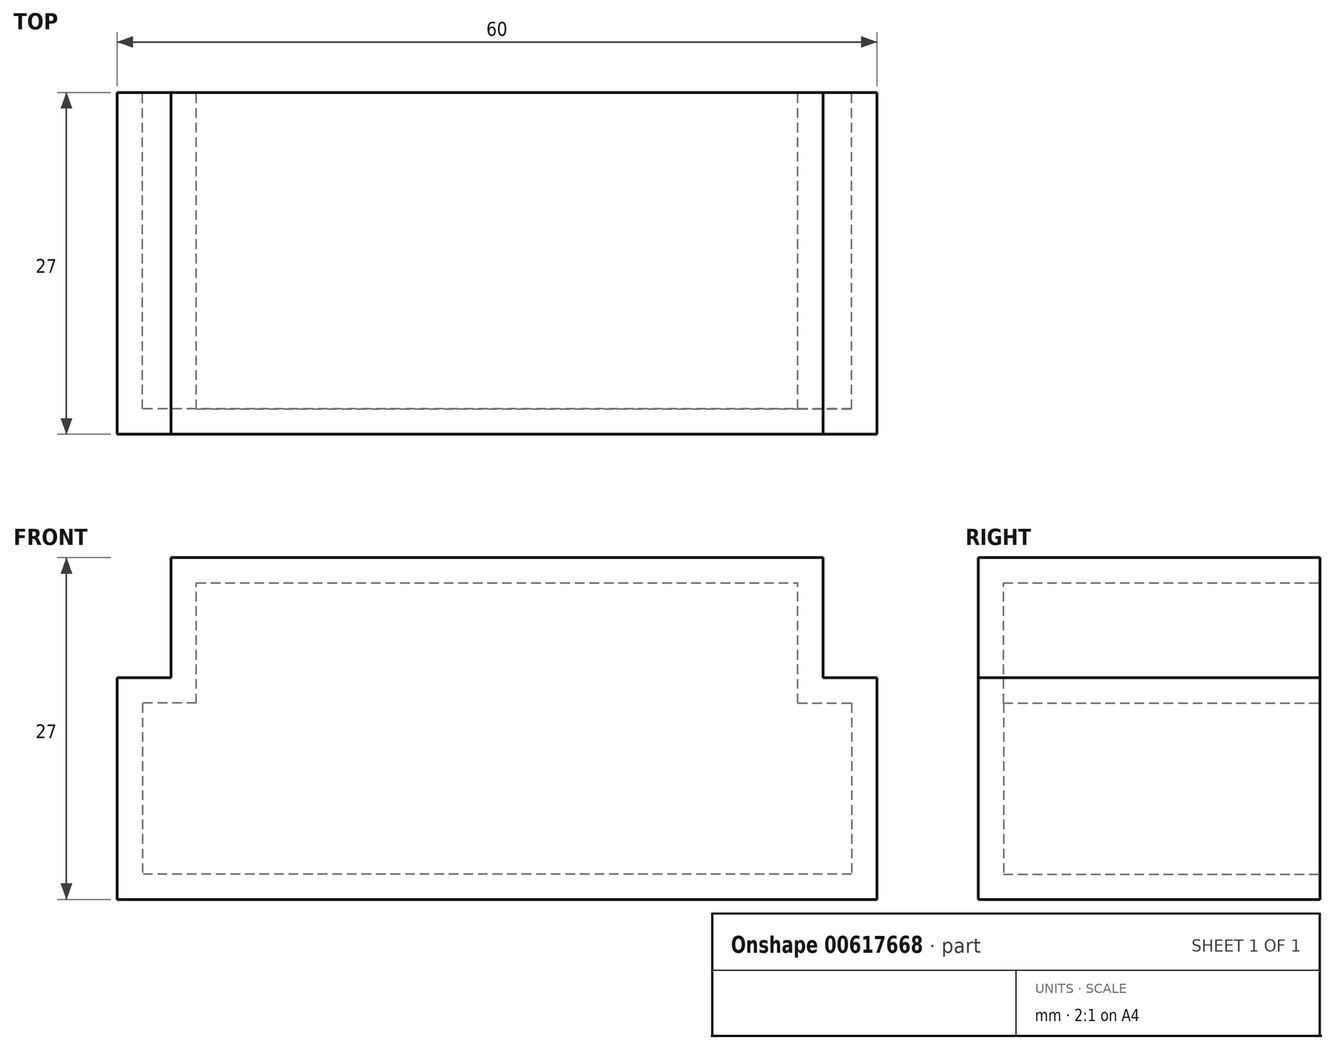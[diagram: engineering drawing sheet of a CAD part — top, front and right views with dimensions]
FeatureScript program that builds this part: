
annotation { "Feature Type Name" : "Feature", "Feature Type Description" : "" }
export const myFeature = defineFeature(function(context is Context, id is Id, definition is map)
    precondition{}
    {
        {
            var Q0;
            Q0=qCreatedBy(makeId("Front.planeOp"),FACE);
            var sketch = newSketch(context, id + "F0", { "sketchPlane" : qUnion([Q0])});
            skLineSegment(sketch, "E0.bottom", {"start": v(0, 0) * mm, "end": v(47.5, 0) * mm});
            skLineSegment(sketch, "E0.top", {"start": v(0, 9.5) * mm, "end": v(47.5, 9.5) * mm});
            skLineSegment(sketch, "E0.left", {"start": v(0, 0) * mm, "end": v(0, 9.5) * mm});
            skLineSegment(sketch, "E0.right", {"start": v(47.5, 0) * mm, "end": v(47.5, 9.5) * mm});
            skLineSegment(sketch, "E1.bottom", {"start": v(0, 9.5) * mm, "end": v(-2, 9.5) * mm});
            skLineSegment(sketch, "E1.top", {"start": v(0, 11.5) * mm, "end": v(-2, 11.5) * mm});
            skLineSegment(sketch, "E1.left", {"start": v(0, 9.5) * mm, "end": v(0, 11.5) * mm});
            skLineSegment(sketch, "E1.right", {"start": v(-2, 9.5) * mm, "end": v(-2, 11.5) * mm});
            skLineSegment(sketch, "E2.bottom", {"start": v(47.5, 9.5) * mm, "end": v(49.5, 9.5) * mm});
            skLineSegment(sketch, "E2.top", {"start": v(47.5, 11.5) * mm, "end": v(49.5, 11.5) * mm});
            skLineSegment(sketch, "E2.left", {"start": v(47.5, 9.5) * mm, "end": v(47.5, 11.5) * mm});
            skLineSegment(sketch, "E2.right", {"start": v(49.5, 9.5) * mm, "end": v(49.5, 11.5) * mm});
            skLineSegment(sketch, "E3", {"start": v(-2, 9.5) * mm, "end": v(-2, 0) * mm});
            skLineSegment(sketch, "E4", {"start": v(0, 11.5) * mm, "end": v(47.5, 11.5) * mm});
            skLineSegment(sketch, "E5", {"start": v(49.5, 11.5) * mm, "end": v(49.5, 0) * mm});
            skLineSegment(sketch, "E6", {"start": v(0, 0) * mm, "end": v(-4.25, 0) * mm});
            skLineSegment(sketch, "E7", {"start": v(-4.25, 0) * mm, "end": v(-4.25, -13.5) * mm});
            skLineSegment(sketch, "E8", {"start": v(47.5, 0) * mm, "end": v(51.75, 0) * mm});
            skLineSegment(sketch, "E9", {"start": v(51.75, 0) * mm, "end": v(51.75, -13.5) * mm});
            skLineSegment(sketch, "E10", {"start": v(51.75, -13.5) * mm, "end": v(-4.25, -13.5) * mm});
            skLineSegment(sketch, "E11.bottom", {"start": v(-4.25, 0) * mm, "end": v(-6.25, 0) * mm});
            skLineSegment(sketch, "E11.top", {"start": v(-4.25, 2) * mm, "end": v(-6.25, 2) * mm});
            skLineSegment(sketch, "E11.left", {"start": v(-4.25, 0) * mm, "end": v(-4.25, 2) * mm});
            skLineSegment(sketch, "E11.right", {"start": v(-6.25, 0) * mm, "end": v(-6.25, 2) * mm});
            skLineSegment(sketch, "E12.bottom", {"start": v(-4.25, -13.5) * mm, "end": v(-6.25, -13.5) * mm});
            skLineSegment(sketch, "E12.top", {"start": v(-4.25, -15.5) * mm, "end": v(-6.25, -15.5) * mm});
            skLineSegment(sketch, "E12.left", {"start": v(-4.25, -13.5) * mm, "end": v(-4.25, -15.5) * mm});
            skLineSegment(sketch, "E12.right", {"start": v(-6.25, -13.5) * mm, "end": v(-6.25, -15.5) * mm});
            skLineSegment(sketch, "E13.bottom", {"start": v(51.75, -13.5) * mm, "end": v(53.75, -13.5) * mm});
            skLineSegment(sketch, "E13.top", {"start": v(51.75, -15.5) * mm, "end": v(53.75, -15.5) * mm});
            skLineSegment(sketch, "E13.left", {"start": v(51.75, -13.5) * mm, "end": v(51.75, -15.5) * mm});
            skLineSegment(sketch, "E13.right", {"start": v(53.75, -13.5) * mm, "end": v(53.75, -15.5) * mm});
            skLineSegment(sketch, "E14.bottom", {"start": v(51.75, 0) * mm, "end": v(53.75, 0) * mm});
            skLineSegment(sketch, "E14.top", {"start": v(51.75, 2) * mm, "end": v(53.75, 2) * mm});
            skLineSegment(sketch, "E14.left", {"start": v(51.75, 0) * mm, "end": v(51.75, 2) * mm});
            skLineSegment(sketch, "E14.right", {"start": v(53.75, 0) * mm, "end": v(53.75, 2) * mm});
            skLineSegment(sketch, "E15", {"start": v(-2, 2) * mm, "end": v(-6.25, 2) * mm});
            skLineSegment(sketch, "E16", {"start": v(-6.25, -15.5) * mm, "end": v(53.75, -15.5) * mm});
            skLineSegment(sketch, "E17", {"start": v(53.75, 2) * mm, "end": v(53.75, -15.5) * mm});
            skLineSegment(sketch, "E18", {"start": v(-6.25, 2) * mm, "end": v(-6.25, -15.5) * mm});
            skSolve(sketch);
        }
        {
            var Q0;
            Q0=makeQuery(id+"F0.imprint","IMPRINT",FACE,{"disambiguationData":[TD([[makeQuery(id+"F0.imprint","IMPRINT",EDGE,{"derivedFrom":sQuery(id+"F0.wireOp",EDGE,"E0.top")}),1.0]])]});
            var Q1;
            Q1=makeQuery(id+"F0.imprint","IMPRINT",FACE,{"disambiguationData":[TD([[makeQuery(id+"F0.imprint","IMPRINT",EDGE,{"derivedFrom":sQuery(id+"F0.wireOp",EDGE,"E1.bottom")}),-1.0]])]});
            var Q2;
            {var subQ5=sQuery(id+"F0.wireOp",EDGE,"E0.left");Q2=makeQuery(id+"F0.imprint","IMPRINT",FACE,{"disambiguationData":[TD([[makeQuery(id+"F0.imprint","IMPRINT",EDGE,{"derivedFrom":subQ5}),1.0]])]});}
            var Q3;
            {var subQ5=sQuery(id+"F0.wireOp",EDGE,"E11.left");Q3=makeQuery(id+"F0.imprint","IMPRINT",FACE,{"disambiguationData":[TD([[makeQuery(id+"F0.imprint","IMPRINT",EDGE,{"derivedFrom":subQ5}),-1.0]])]});}
            var Q4;
            {var subQ0=sQuery(id+"F0.wireOp",EDGE,"E11.bottom");Q4=makeQuery(id+"F0.imprint","IMPRINT",FACE,{"disambiguationData":[TD([[makeQuery(id+"F0.imprint","IMPRINT",EDGE,{"derivedFrom":subQ0}),-1.0]])]});}
            var Q5;
            Q5=makeQuery(id+"F0.imprint","IMPRINT",FACE,{"disambiguationData":[TD([[makeQuery(id+"F0.imprint","IMPRINT",EDGE,{"derivedFrom":sQuery(id+"F0.wireOp",EDGE,"E7")}),-1.0]])]});
            var Q6;
            {var subQ0=sQuery(id+"F0.wireOp",EDGE,"E12.bottom");Q6=makeQuery(id+"F0.imprint","IMPRINT",FACE,{"disambiguationData":[TD([[makeQuery(id+"F0.imprint","IMPRINT",EDGE,{"derivedFrom":subQ0}),1.0]])]});}
            var Q7;
            Q7=makeQuery(id+"F0.imprint","IMPRINT",FACE,{"disambiguationData":[TD([[makeQuery(id+"F0.imprint","IMPRINT",EDGE,{"derivedFrom":sQuery(id+"F0.wireOp",EDGE,"E10")}),1.0]])]});
            var Q8;
            {var subQ0=sQuery(id+"F0.wireOp",EDGE,"E13.bottom");Q8=makeQuery(id+"F0.imprint","IMPRINT",FACE,{"disambiguationData":[TD([[makeQuery(id+"F0.imprint","IMPRINT",EDGE,{"derivedFrom":subQ0}),-1.0]])]});}
            var Q9;
            Q9=makeQuery(id+"F0.imprint","IMPRINT",FACE,{"disambiguationData":[TD([[makeQuery(id+"F0.imprint","IMPRINT",EDGE,{"derivedFrom":sQuery(id+"F0.wireOp",EDGE,"E9")}),1.0]])]});
            var Q10;
            {var subQ0=sQuery(id+"F0.wireOp",EDGE,"E14.bottom");Q10=makeQuery(id+"F0.imprint","IMPRINT",FACE,{"disambiguationData":[TD([[makeQuery(id+"F0.imprint","IMPRINT",EDGE,{"derivedFrom":subQ0}),1.0]])]});}
            var Q11;
            {var subQ0=sQuery(id+"F0.wireOp",EDGE,"E0.right");Q11=makeQuery(id+"F0.imprint","IMPRINT",FACE,{"disambiguationData":[TD([[makeQuery(id+"F0.imprint","IMPRINT",EDGE,{"derivedFrom":subQ0}),-1.0]])]});}
            var Q12;
            {var subQ0=sQuery(id+"F0.wireOp",EDGE,"E2.bottom");Q12=makeQuery(id+"F0.imprint","IMPRINT",FACE,{"disambiguationData":[TD([[makeQuery(id+"F0.imprint","IMPRINT",EDGE,{"derivedFrom":subQ0}),1.0]])]});}
            extrude(context, id + "F1", {"entities" : qUnion([Q0, Q1, Q2, Q3, Q4, Q5, Q6, Q7, Q8, Q9, Q10, Q11, Q12]), "depth" : 25 * mm, "offsetDistance" : 25 * mm});
        }
        {
            var Q0;
            Q0=makeQuery(id+"F1.opExtrude","CAP_FACE",FACE,{"disambiguationData":[OSD([sQuery(id+"F0.wireOp",EDGE,"E0.top"),sQuery(id+"F0.wireOp",EDGE,"E0.left"),sQuery(id+"F0.wireOp",EDGE,"E0.right"),sQuery(id+"F0.wireOp",EDGE,"E1.top"),sQuery(id+"F0.wireOp",EDGE,"E1.right"),sQuery(id+"F0.wireOp",EDGE,"E2.top"),sQuery(id+"F0.wireOp",EDGE,"E3"),sQuery(id+"F0.wireOp",EDGE,"E4"),sQuery(id+"F0.wireOp",EDGE,"E5"),sQuery(id+"F0.wireOp",EDGE,"E6"),sQuery(id+"F0.wireOp",EDGE,"E7"),sQuery(id+"F0.wireOp",EDGE,"E8"),sQuery(id+"F0.wireOp",EDGE,"E9"),sQuery(id+"F0.wireOp",EDGE,"E10"),sQuery(id+"F0.wireOp",EDGE,"E14.top"),sQuery(id+"F0.wireOp",EDGE,"E14.left"),sQuery(id+"F0.wireOp",EDGE,"E15"),sQuery(id+"F0.wireOp",EDGE,"E16"),sQuery(id+"F0.wireOp",EDGE,"E17"),sQuery(id+"F0.wireOp",EDGE,"E18")])],"isStart":false});
            var sketch = newSketch(context, id + "F2", { "sketchPlane" : qUnion([Q0])});
            skLineSegment(sketch, "E19.bottom", {"start": v(47.5, 0) * mm, "end": v(53.75, 0) * mm});
            skLineSegment(sketch, "E19.top", {"start": v(47.5, 2) * mm, "end": v(53.75, 2) * mm});
            skLineSegment(sketch, "E19.left", {"start": v(47.5, 0) * mm, "end": v(47.5, 2) * mm});
            skLineSegment(sketch, "E19.right", {"start": v(53.75, 0) * mm, "end": v(53.75, 2) * mm});
            skSolve(sketch);
        }
        {
            var Q0;
            Q0 = qSketchRegion(id + "F2", true);
            extrude(context, id + "F3", {"entities" : qUnion([Q0]), "operationType" : NewBodyOperationType.ADD, "oppositeDirection" : true, "depth" : 25 * mm, "offsetDistance" : 25 * mm});
        }
        {
            var Q0;
            Q0=makeQuery(id+"F3.boolean.opBoolean","MERGE",FACE,{"derivedFrom":[makeQuery(id+"F1.opExtrude","CAP_FACE",FACE,{"disambiguationData":[OSD([sQuery(id+"F0.wireOp",EDGE,"E0.top"),sQuery(id+"F0.wireOp",EDGE,"E0.left"),sQuery(id+"F0.wireOp",EDGE,"E0.right"),sQuery(id+"F0.wireOp",EDGE,"E1.top"),sQuery(id+"F0.wireOp",EDGE,"E1.right"),sQuery(id+"F0.wireOp",EDGE,"E2.top"),sQuery(id+"F0.wireOp",EDGE,"E3"),sQuery(id+"F0.wireOp",EDGE,"E4"),sQuery(id+"F0.wireOp",EDGE,"E5"),sQuery(id+"F0.wireOp",EDGE,"E6"),sQuery(id+"F0.wireOp",EDGE,"E7"),sQuery(id+"F0.wireOp",EDGE,"E8"),sQuery(id+"F0.wireOp",EDGE,"E9"),sQuery(id+"F0.wireOp",EDGE,"E10"),sQuery(id+"F0.wireOp",EDGE,"E14.top"),sQuery(id+"F0.wireOp",EDGE,"E14.left"),sQuery(id+"F0.wireOp",EDGE,"E15"),sQuery(id+"F0.wireOp",EDGE,"E16"),sQuery(id+"F0.wireOp",EDGE,"E17"),sQuery(id+"F0.wireOp",EDGE,"E18")])],"isStart":false}),makeQuery(id+"F3.opExtrude","CAP_FACE",FACE,{"disambiguationData":[OSD([sQuery(id+"F2.wireOp",EDGE,"E19.bottom"),sQuery(id+"F2.wireOp",EDGE,"E19.top"),sQuery(id+"F2.wireOp",EDGE,"E19.left"),sQuery(id+"F2.wireOp",EDGE,"E19.right")])],"isStart":true})]});
            var sketch = newSketch(context, id + "F4", { "sketchPlane" : qUnion([Q0])});
            skLineSegment(sketch, "E20.bottom", {"start": v(-6.25, -15.5) * mm, "end": v(53.75, -15.5) * mm});
            skLineSegment(sketch, "E20.top", {"start": v(-6.25, 2) * mm, "end": v(53.75, 2) * mm});
            skLineSegment(sketch, "E20.left", {"start": v(-6.25, -15.5) * mm, "end": v(-6.25, 2) * mm});
            skLineSegment(sketch, "E20.right", {"start": v(53.75, -15.5) * mm, "end": v(53.75, 2) * mm});
            skLineSegment(sketch, "E21.bottom", {"start": v(49.5, 2) * mm, "end": v(-2, 2) * mm});
            skLineSegment(sketch, "E21.top", {"start": v(49.5, 11.5) * mm, "end": v(-2, 11.5) * mm});
            skLineSegment(sketch, "E21.left", {"start": v(49.5, 2) * mm, "end": v(49.5, 11.5) * mm});
            skLineSegment(sketch, "E21.right", {"start": v(-2, 2) * mm, "end": v(-2, 11.5) * mm});
            skSolve(sketch);
        }
        {
            var Q0;
            Q0 = qSketchRegion(id + "F4", true);
            extrude(context, id + "F5", {"entities" : qUnion([Q0]), "operationType" : NewBodyOperationType.ADD, "depth" : 2 * mm, "offsetDistance" : 25 * mm});
        }
    });
